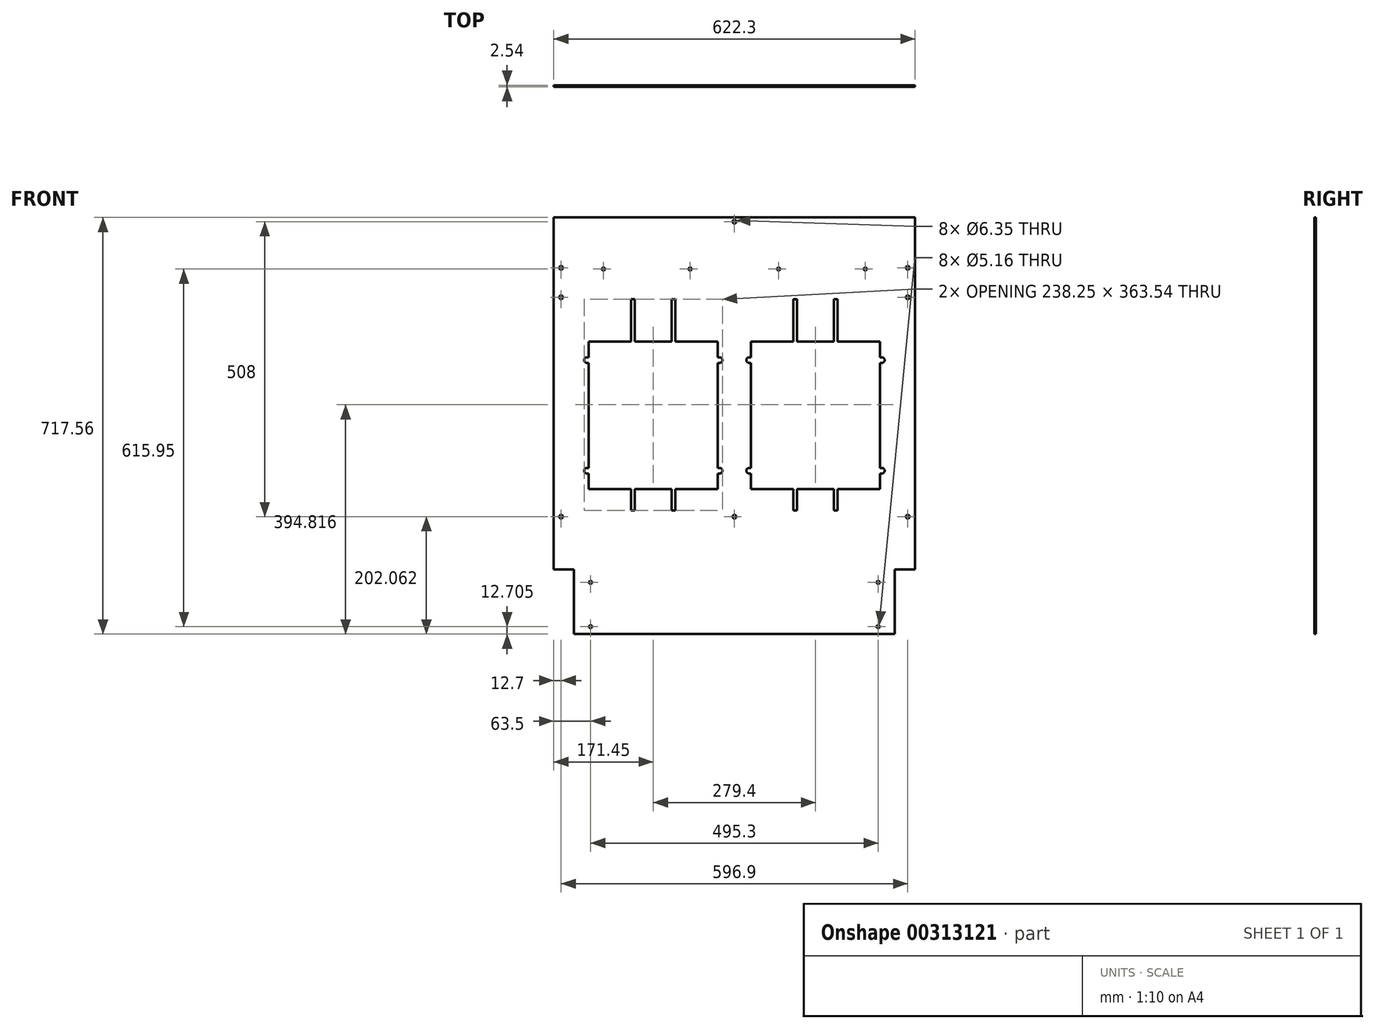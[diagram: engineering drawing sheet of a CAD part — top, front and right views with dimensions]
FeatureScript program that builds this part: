
annotation { "Feature Type Name" : "Feature", "Feature Type Description" : "" }
export const myFeature = defineFeature(function(context is Context, id is Id, definition is map)
    precondition{}
    {
        {
            var Q0;
            Q0=qCreatedBy(makeId("Front.planeOp"),FACE);
            var sketch = newSketch(context, id + "F0", { "sketchPlane" : qUnion([Q0])});
            skLineSegment(sketch, "E0.bottom", {"start": v(-311.15, 358.77) * mm, "end": v(311.15, 358.78) * mm});
            skLineSegment(sketch, "E0.top", {"start": v(-311.15, -358.78) * mm, "end": v(311.15, -358.77) * mm});
            skLineSegment(sketch, "E0.left", {"start": v(-311.15, 358.77) * mm, "end": v(-311.15, -358.78) * mm});
            skLineSegment(sketch, "E0.right", {"start": v(311.15, 358.78) * mm, "end": v(311.15, -358.77) * mm});
            skLineSegment(sketch, "E1.bottom", {"start": v(-250.83, 144.78) * mm, "end": v(-28.58, 144.78) * mm});
            skLineSegment(sketch, "E1.top", {"start": v(-250.83, -109.22) * mm, "end": v(-28.58, -109.22) * mm});
            skLineSegment(sketch, "E1.left", {"start": v(-250.83, 144.78) * mm, "end": v(-250.83, 117.86) * mm});
            skLineSegment(sketch, "E1.right", {"start": v(-28.58, 144.78) * mm, "end": v(-28.58, 117.86) * mm});
            skPoint(sketch, "E1.middle", {"position": v(-139.7, 17.78) * mm});
            skLineSegment(sketch, "E2", {"start": v(0, 0) * mm, "end": v(0, 17.78) * mm, "construction": true});
            skLineSegment(sketch, "E3", {"start": v(-139.7, 17.78) * mm, "end": v(0, 17.78) * mm, "construction": true});
            skArc(sketch, "E4", {"start": v(-254, 117.86) * mm, "mid": v(-258.83, 113.03) * mm, "end": v(-254, 108.2) * mm});
            skArc(sketch, "E5", {"start": v(-25.4, 108.2) * mm, "mid": v(-20.57, 113.03) * mm, "end": v(-25.4, 117.86) * mm});
            skArc(sketch, "E6", {"start": v(-25.4, -82.3) * mm, "mid": v(-20.57, -77.47) * mm, "end": v(-25.4, -72.64) * mm});
            skArc(sketch, "E7", {"start": v(-254, -72.64) * mm, "mid": v(-258.83, -77.47) * mm, "end": v(-254, -82.3) * mm});
            skLineSegment(sketch, "E8", {"start": v(-25.4, 117.86) * mm, "end": v(-28.58, 117.86) * mm});
            skLineSegment(sketch, "E9", {"start": v(-25.4, 108.2) * mm, "end": v(-28.58, 108.2) * mm});
            skLineSegment(sketch, "E10.trimOffspring", {"start": v(-28.58, 108.2) * mm, "end": v(-28.58, -72.64) * mm});
            skLineSegment(sketch, "E11", {"start": v(-25.4, -72.64) * mm, "end": v(-28.58, -72.64) * mm});
            skLineSegment(sketch, "E12", {"start": v(-25.4, -82.3) * mm, "end": v(-28.58, -82.3) * mm});
            skLineSegment(sketch, "E13.trimOffspring", {"start": v(-28.58, -82.3) * mm, "end": v(-28.58, -109.22) * mm});
            skLineSegment(sketch, "E14", {"start": v(-254, -72.64) * mm, "end": v(-250.83, -72.64) * mm});
            skLineSegment(sketch, "E15", {"start": v(-254, -82.3) * mm, "end": v(-250.83, -82.3) * mm});
            skLineSegment(sketch, "E16", {"start": v(-254, 117.86) * mm, "end": v(-250.83, 117.86) * mm});
            skLineSegment(sketch, "E17", {"start": v(-254, 108.2) * mm, "end": v(-250.83, 108.2) * mm});
            skLineSegment(sketch, "E18.trimOffspring", {"start": v(-250.83, 108.2) * mm, "end": v(-250.83, -72.64) * mm});
            skLineSegment(sketch, "E19.trimOffspring", {"start": v(-250.83, -82.3) * mm, "end": v(-250.83, -109.22) * mm});
            skLineSegment(sketch, "E20.1.0.0", {"start": v(28.57, -82.3) * mm, "end": v(28.57, -109.22) * mm});
            skLineSegment(sketch, "E20.1.0.1", {"start": v(250.82, 108.2) * mm, "end": v(250.82, -72.64) * mm});
            skLineSegment(sketch, "E20.1.0.2", {"start": v(139.7, 17.78) * mm, "end": v(279.4, 17.78) * mm, "construction": true});
            skLineSegment(sketch, "E20.1.0.3", {"start": v(250.82, 144.78) * mm, "end": v(250.82, 117.86) * mm});
            skLineSegment(sketch, "E20.1.0.4", {"start": v(250.82, -82.3) * mm, "end": v(250.82, -109.22) * mm});
            skPoint(sketch, "E20.1.0.5", {"position": v(139.7, 17.78) * mm});
            skLineSegment(sketch, "E20.1.0.6", {"start": v(28.57, 144.78) * mm, "end": v(250.82, 144.78) * mm});
            skLineSegment(sketch, "E20.1.0.7", {"start": v(28.57, -109.22) * mm, "end": v(250.82, -109.22) * mm});
            skLineSegment(sketch, "E20.1.0.8", {"start": v(28.57, 108.2) * mm, "end": v(28.57, -72.64) * mm});
            skLineSegment(sketch, "E20.1.0.9", {"start": v(28.57, 144.78) * mm, "end": v(28.57, 117.86) * mm});
            skLineSegment(sketch, "E20.1.0.10", {"start": v(25.4, -72.64) * mm, "end": v(28.57, -72.64) * mm});
            skLineSegment(sketch, "E20.1.0.11", {"start": v(25.4, 117.86) * mm, "end": v(28.57, 117.86) * mm});
            skArc(sketch, "E20.1.0.12", {"start": v(254, -82.3) * mm, "mid": v(258.83, -77.47) * mm, "end": v(254, -72.64) * mm});
            skLineSegment(sketch, "E20.1.0.13", {"start": v(254, -82.3) * mm, "end": v(250.82, -82.3) * mm});
            skLineSegment(sketch, "E20.1.0.14", {"start": v(25.4, -82.3) * mm, "end": v(28.57, -82.3) * mm});
            skLineSegment(sketch, "E20.1.0.15", {"start": v(254, -72.64) * mm, "end": v(250.82, -72.64) * mm});
            skArc(sketch, "E20.1.0.16", {"start": v(25.4, -72.64) * mm, "mid": v(20.57, -77.47) * mm, "end": v(25.4, -82.3) * mm});
            skLineSegment(sketch, "E20.1.0.17", {"start": v(254, 117.86) * mm, "end": v(250.82, 117.86) * mm});
            skLineSegment(sketch, "E20.1.0.18", {"start": v(254, 108.2) * mm, "end": v(250.82, 108.2) * mm});
            skArc(sketch, "E20.1.0.19", {"start": v(254, 108.2) * mm, "mid": v(258.83, 113.03) * mm, "end": v(254, 117.86) * mm});
            skLineSegment(sketch, "E20.1.0.20", {"start": v(25.4, 108.2) * mm, "end": v(28.57, 108.2) * mm});
            skArc(sketch, "E20.1.0.21", {"start": v(25.4, 117.86) * mm, "mid": v(20.57, 113.03) * mm, "end": v(25.4, 108.2) * mm});
            skLineSegment(sketch, "E20.direction1", {"start": v(-250.83, -109.22) * mm, "end": v(28.57, -109.22) * mm, "construction": true});
            skCircle(sketch, "E21", {"center": v(-298.45, 221.1) * mm, "radius": 3.18 * mm});
            skCircle(sketch, "E22", {"center": v(-298.45, 271.9) * mm, "radius": 3.18 * mm});
            skCircle(sketch, "E23", {"center": v(298.45, 271.9) * mm, "radius": 3.18 * mm});
            skCircle(sketch, "E24", {"center": v(298.45, 221.1) * mm, "radius": 3.18 * mm});
            skCircle(sketch, "E25", {"center": v(-298.45, -156.72) * mm, "radius": 3.18 * mm});
            skCircle(sketch, "E26", {"center": v(298.45, -156.72) * mm, "radius": 3.18 * mm});
            skCircle(sketch, "E27", {"center": v(0, -156.72) * mm, "radius": 3.18 * mm});
            skCircle(sketch, "E28", {"center": v(0, 351.28) * mm, "radius": 3.18 * mm});
            skPoint(sketch, "E28.centerSnap0", {"position": v(0, 8.9) * mm});
            skCircle(sketch, "E29", {"center": v(-247.65, -346.08) * mm, "radius": 2.58 * mm});
            skCircle(sketch, "E30", {"center": v(-247.65, -269.88) * mm, "radius": 2.58 * mm});
            skCircle(sketch, "E31", {"center": v(247.65, -346.08) * mm, "radius": 2.58 * mm});
            skCircle(sketch, "E32", {"center": v(247.65, -269.88) * mm, "radius": 2.58 * mm});
            skSolve(sketch);
        }
        {
            var Q0;
            Q0=qSketchRegion(id+"F0",true);
            extrude(context, id + "F1", {"entities" : qUnion([Q0]), "endBound" : BoundingType.SYMMETRIC, "depth" : 2.54 * mm});
        }
        {
            var Q0;
            Q0=makeQuery(id+"F1.opExtrude","CAP_FACE",FACE,{"disambiguationData":[OSD([sQuery(id+"F0.wireOp",EDGE,"E0.bottom"),sQuery(id+"F0.wireOp",EDGE,"E0.top"),sQuery(id+"F0.wireOp",EDGE,"E0.left"),sQuery(id+"F0.wireOp",EDGE,"E0.right"),sQuery(id+"F0.wireOp",EDGE,"E1.bottom"),sQuery(id+"F0.wireOp",EDGE,"E1.top"),sQuery(id+"F0.wireOp",EDGE,"E1.left"),sQuery(id+"F0.wireOp",EDGE,"E1.right"),sQuery(id+"F0.wireOp",EDGE,"E4"),sQuery(id+"F0.wireOp",EDGE,"E5"),sQuery(id+"F0.wireOp",EDGE,"E6"),sQuery(id+"F0.wireOp",EDGE,"E7"),sQuery(id+"F0.wireOp",EDGE,"E8"),sQuery(id+"F0.wireOp",EDGE,"E9"),sQuery(id+"F0.wireOp",EDGE,"E10.trimOffspring"),sQuery(id+"F0.wireOp",EDGE,"E11"),sQuery(id+"F0.wireOp",EDGE,"E12"),sQuery(id+"F0.wireOp",EDGE,"E13.trimOffspring"),sQuery(id+"F0.wireOp",EDGE,"E14"),sQuery(id+"F0.wireOp",EDGE,"E15"),sQuery(id+"F0.wireOp",EDGE,"E16"),sQuery(id+"F0.wireOp",EDGE,"E17"),sQuery(id+"F0.wireOp",EDGE,"E18.trimOffspring"),sQuery(id+"F0.wireOp",EDGE,"E19.trimOffspring"),sQuery(id+"F0.wireOp",EDGE,"E20.1.0.0"),sQuery(id+"F0.wireOp",EDGE,"E20.1.0.1"),sQuery(id+"F0.wireOp",EDGE,"E20.1.0.3"),sQuery(id+"F0.wireOp",EDGE,"E20.1.0.4"),sQuery(id+"F0.wireOp",EDGE,"E20.1.0.6"),sQuery(id+"F0.wireOp",EDGE,"E20.1.0.7"),sQuery(id+"F0.wireOp",EDGE,"E20.1.0.8"),sQuery(id+"F0.wireOp",EDGE,"E20.1.0.9"),sQuery(id+"F0.wireOp",EDGE,"E20.1.0.10"),sQuery(id+"F0.wireOp",EDGE,"E20.1.0.11"),sQuery(id+"F0.wireOp",EDGE,"E20.1.0.12"),sQuery(id+"F0.wireOp",EDGE,"E20.1.0.13"),sQuery(id+"F0.wireOp",EDGE,"E20.1.0.14"),sQuery(id+"F0.wireOp",EDGE,"E20.1.0.15"),sQuery(id+"F0.wireOp",EDGE,"E20.1.0.16"),sQuery(id+"F0.wireOp",EDGE,"E20.1.0.17"),sQuery(id+"F0.wireOp",EDGE,"E20.1.0.18"),sQuery(id+"F0.wireOp",EDGE,"E20.1.0.19"),sQuery(id+"F0.wireOp",EDGE,"E20.1.0.20"),sQuery(id+"F0.wireOp",EDGE,"E20.1.0.21")])],"isStart":false});
            var sketch = newSketch(context, id + "F2", { "sketchPlane" : qUnion([Q0])});
            skLineSegment(sketch, "E33.bottom", {"start": v(-276.23, -358.78) * mm, "end": v(-311.15, -358.78) * mm});
            skLineSegment(sketch, "E33.top", {"start": v(-276.23, -247.65) * mm, "end": v(-311.15, -247.65) * mm});
            skLineSegment(sketch, "E33.left", {"start": v(-276.23, -358.78) * mm, "end": v(-276.23, -247.65) * mm});
            skLineSegment(sketch, "E33.right", {"start": v(-311.15, -358.78) * mm, "end": v(-311.15, -247.65) * mm});
            skLineSegment(sketch, "E34.bottom", {"start": v(311.15, -358.77) * mm, "end": v(276.23, -358.77) * mm});
            skLineSegment(sketch, "E34.top", {"start": v(311.15, -247.65) * mm, "end": v(276.23, -247.65) * mm});
            skLineSegment(sketch, "E34.left", {"start": v(311.15, -358.77) * mm, "end": v(311.15, -247.65) * mm});
            skLineSegment(sketch, "E34.right", {"start": v(276.23, -358.77) * mm, "end": v(276.23, -247.65) * mm});
            skLineSegment(sketch, "E35.bottom", {"start": v(-177.8, 144.78) * mm, "end": v(-171.45, 144.78) * mm});
            skLineSegment(sketch, "E35.top", {"start": v(-177.8, 217.8) * mm, "end": v(-171.45, 217.8) * mm});
            skLineSegment(sketch, "E35.left", {"start": v(-177.8, 144.78) * mm, "end": v(-177.8, 217.8) * mm});
            skLineSegment(sketch, "E35.right", {"start": v(-171.45, 144.78) * mm, "end": v(-171.45, 217.8) * mm});
            skLineSegment(sketch, "E36.bottom", {"start": v(-107.95, 144.78) * mm, "end": v(-101.6, 144.78) * mm});
            skLineSegment(sketch, "E36.top", {"start": v(-107.95, 217.8) * mm, "end": v(-101.6, 217.8) * mm});
            skLineSegment(sketch, "E36.left", {"start": v(-107.95, 144.78) * mm, "end": v(-107.95, 217.8) * mm});
            skLineSegment(sketch, "E36.right", {"start": v(-101.6, 144.78) * mm, "end": v(-101.6, 217.8) * mm});
            skLineSegment(sketch, "E37.bottom", {"start": v(-107.95, -109.22) * mm, "end": v(-101.6, -109.22) * mm});
            skLineSegment(sketch, "E37.top", {"start": v(-107.95, -145.73) * mm, "end": v(-101.6, -145.73) * mm});
            skLineSegment(sketch, "E37.left", {"start": v(-107.95, -109.22) * mm, "end": v(-107.95, -145.73) * mm});
            skLineSegment(sketch, "E37.right", {"start": v(-101.6, -109.22) * mm, "end": v(-101.6, -145.73) * mm});
            skLineSegment(sketch, "E38.bottom", {"start": v(-171.45, -109.22) * mm, "end": v(-177.8, -109.22) * mm});
            skLineSegment(sketch, "E38.top", {"start": v(-171.45, -145.73) * mm, "end": v(-177.8, -145.73) * mm});
            skLineSegment(sketch, "E38.left", {"start": v(-171.45, -109.22) * mm, "end": v(-171.45, -145.73) * mm});
            skLineSegment(sketch, "E38.right", {"start": v(-177.8, -109.22) * mm, "end": v(-177.8, -145.73) * mm});
            skLineSegment(sketch, "E39.1.0.0", {"start": v(101.6, 144.78) * mm, "end": v(101.6, 217.8) * mm});
            skLineSegment(sketch, "E39.1.0.1", {"start": v(107.95, 144.78) * mm, "end": v(107.95, 217.8) * mm});
            skLineSegment(sketch, "E39.1.0.2", {"start": v(171.45, -109.22) * mm, "end": v(171.45, -145.73) * mm});
            skLineSegment(sketch, "E39.1.0.3", {"start": v(177.8, -109.22) * mm, "end": v(177.8, -145.73) * mm});
            skLineSegment(sketch, "E39.1.0.4", {"start": v(171.45, 144.78) * mm, "end": v(171.45, 217.8) * mm});
            skLineSegment(sketch, "E39.1.0.5", {"start": v(177.8, 144.78) * mm, "end": v(177.8, 217.8) * mm});
            skLineSegment(sketch, "E39.1.0.6", {"start": v(101.6, -109.22) * mm, "end": v(101.6, -145.73) * mm});
            skLineSegment(sketch, "E39.1.0.7", {"start": v(107.95, -109.22) * mm, "end": v(107.95, -145.73) * mm});
            skLineSegment(sketch, "E39.1.0.8", {"start": v(171.45, -145.73) * mm, "end": v(177.8, -145.73) * mm});
            skLineSegment(sketch, "E39.1.0.9", {"start": v(101.6, 217.8) * mm, "end": v(107.95, 217.8) * mm});
            skLineSegment(sketch, "E39.1.0.10", {"start": v(107.95, -109.22) * mm, "end": v(101.6, -109.22) * mm});
            skLineSegment(sketch, "E39.1.0.11", {"start": v(101.6, 144.78) * mm, "end": v(107.95, 144.78) * mm});
            skLineSegment(sketch, "E39.1.0.12", {"start": v(171.45, 144.78) * mm, "end": v(177.8, 144.78) * mm});
            skLineSegment(sketch, "E39.1.0.13", {"start": v(171.45, 217.8) * mm, "end": v(177.8, 217.8) * mm});
            skLineSegment(sketch, "E39.1.0.14", {"start": v(171.45, -109.22) * mm, "end": v(177.8, -109.22) * mm});
            skLineSegment(sketch, "E39.1.0.15", {"start": v(107.95, -145.73) * mm, "end": v(101.6, -145.73) * mm});
            skLineSegment(sketch, "E39.direction1", {"start": v(-177.8, -145.73) * mm, "end": v(101.6, -145.73) * mm, "construction": true});
            skPoint(sketch, "E40", {"position": v(-104.78, 144.78) * mm});
            skPoint(sketch, "E41", {"position": v(-174.63, 144.78) * mm});
            skCircle(sketch, "E42", {"center": v(225.42, 269.88) * mm, "radius": 2.58 * mm});
            skCircle(sketch, "E43", {"center": v(-225.42, 269.88) * mm, "radius": 2.58 * mm});
            skLineSegment(sketch, "E44", {"start": v(225.42, 269.88) * mm, "end": v(-225.42, 269.88) * mm, "construction": true});
            skPoint(sketch, "E45", {"position": v(0, 269.88) * mm});
            skCircle(sketch, "E46", {"center": v(76.2, 269.88) * mm, "radius": 2.58 * mm});
            skCircle(sketch, "E47", {"center": v(-76.2, 269.88) * mm, "radius": 2.58 * mm});
            skLineSegment(sketch, "E48.direction1", {"start": v(-225.42, 269.88) * mm, "end": v(-76.2, 269.88) * mm, "construction": true});
            skLineSegment(sketch, "E49.direction1", {"start": v(-225.43, 269.88) * mm, "end": v(0, 269.88) * mm, "construction": true});
            skSolve(sketch);
        }
        {
            var Q0;
            Q0 = qSketchRegion(id + "F2", true);
            extrude(context, id + "F3", {"entities" : qUnion([Q0]), "operationType" : NewBodyOperationType.REMOVE, "endBound" : BoundingType.THROUGH_ALL, "oppositeDirection" : true, "depth" : 25.4 * mm});
        }
    });
